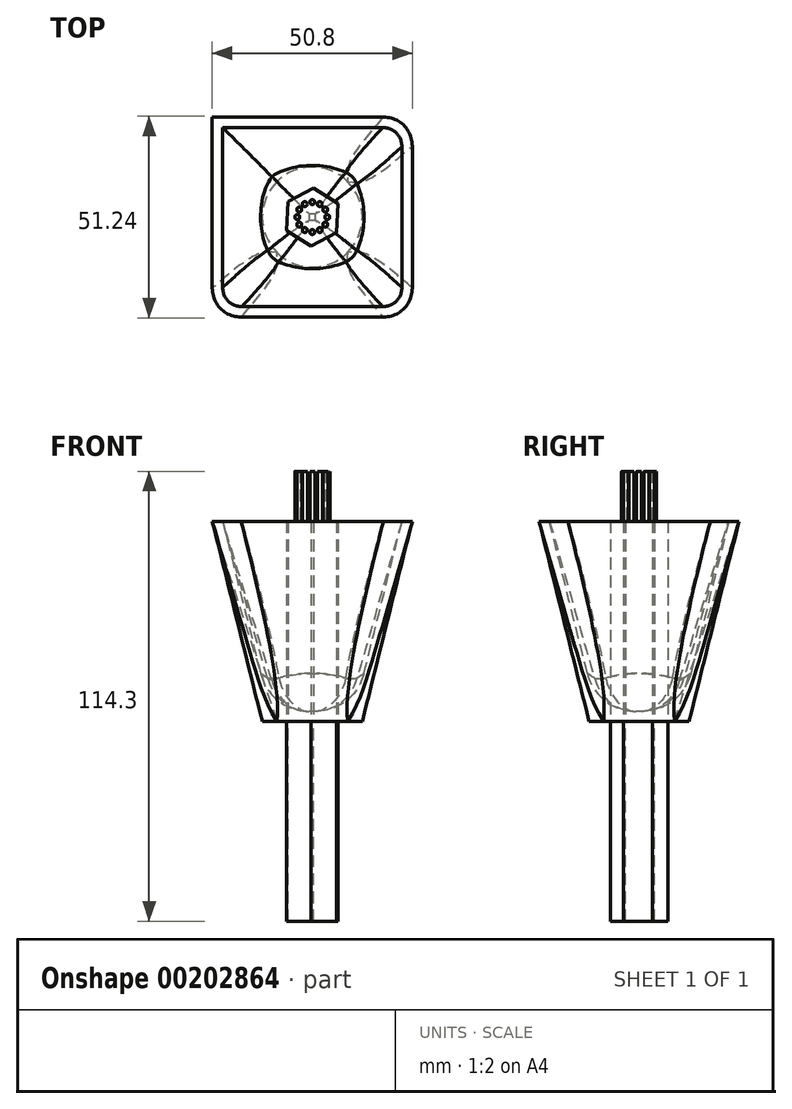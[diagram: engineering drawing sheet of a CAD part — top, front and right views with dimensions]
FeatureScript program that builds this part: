
annotation { "Feature Type Name" : "Feature", "Feature Type Description" : "" }
export const myFeature = defineFeature(function(context is Context, id is Id, definition is map)
    precondition{}
    {
        {
            var Q0;
            Q0=qCreatedBy(makeId("Top.planeOp"),FACE);
            var sketch = newSketch(context, id + "F0", { "sketchPlane" : qUnion([Q0])});
            skCircle(sketch, "E0", {"center": v(0, 0) * mm, "radius": 12.7 * mm});
            skSolve(sketch);
        }
        {
            var Q0;
            Q0=qCreatedBy(makeId("Top.planeOp"),FACE);
            cPlane(context, id + "F1", {"entities" : qUnion([Q0]), "cplaneType" : CPlaneType.OFFSET, "offset" : 50.8 * mm, "width" : 152.4 * mm, "height" : 152.4 * mm});
        }
        {
            var Q0;
            Q0=qCreatedBy(id+"F1.planeOp",FACE);
            var sketch = newSketch(context, id + "F2", { "sketchPlane" : qUnion([Q0])});
            skLineSegment(sketch, "E1.bottom", {"start": v(25.4, 25.4) * mm, "end": v(-25.4, 25.4) * mm});
            skLineSegment(sketch, "E1.top", {"start": v(25.4, -25.4) * mm, "end": v(-25.4, -25.4) * mm});
            skLineSegment(sketch, "E1.left", {"start": v(25.4, 25.4) * mm, "end": v(25.4, -25.4) * mm});
            skLineSegment(sketch, "E1.right", {"start": v(-25.4, 25.4) * mm, "end": v(-25.4, -25.4) * mm});
            skPoint(sketch, "E1.middle", {"position": v(0, 0) * mm});
            skSolve(sketch);
        }
        {
            var Q0;
            Q0=makeQuery(id+"F0.imprint","IMPRINT",FACE,{"disambiguationData":[TD([[makeQuery(id+"F0.imprint","IMPRINT",EDGE,{"derivedFrom":sQuery(id+"F0.wireOp",EDGE,"E0")}),1.0]])]});
            var Q1;
            Q1=makeQuery(id+"F2.imprint","IMPRINT",FACE,{"disambiguationData":[TD([[makeQuery(id+"F2.imprint","IMPRINT",EDGE,{"derivedFrom":sQuery(id+"F2.wireOp",EDGE,"E1.bottom")}),1.0]])]});
            loft(context, id + "F3", {"sheetProfilesArray" : [{ "sheetProfileEntities" : qUnion([Q0]) }, { "sheetProfileEntities" : qUnion([Q1]) }]});
        }
        {
            var Q0;
            Q0=makeQuery(id+"F3.opLoft","SWEPT_EDGE",EDGE,{"disambiguationData":[OSD([sQuery(id+"F0.wireOp",EDGE,"E0"),sQuery(id+"F2.wireOp",EDGE,"E1.bottom"),sQuery(id+"F2.wireOp",EDGE,"E1.left"),sQuery(id+"F2.wireOp",EDGE,"E1.right")])]});
            var Q1;
            Q1=makeQuery(id+"F3.opLoft","SWEPT_EDGE",EDGE,{"disambiguationData":[OSD([sQuery(id+"F2.wireOp",EDGE,"E1.bottom"),sQuery(id+"F2.wireOp",EDGE,"E1.left")])]});
            var Q2;
            Q2=makeQuery(id+"F3.opLoft","SWEPT_EDGE",EDGE,{"disambiguationData":[OSD([sQuery(id+"F0.wireOp",EDGE,"E0"),sQuery(id+"F2.wireOp",EDGE,"E1.top"),sQuery(id+"F2.wireOp",EDGE,"E1.left"),sQuery(id+"F2.wireOp",EDGE,"E1.right")])]});
            var Q3;
            Q3=makeQuery(id+"F3.opLoft","SWEPT_EDGE",EDGE,{"disambiguationData":[OSD([sQuery(id+"F0.wireOp",EDGE,"E0"),sQuery(id+"F2.wireOp",EDGE,"E1.bottom"),sQuery(id+"F2.wireOp",EDGE,"E1.top"),sQuery(id+"F2.wireOp",EDGE,"E1.right")])]});
            fillet(context, id + "F4", {"entities" : qUnion([Q0, Q1, Q2, Q3]), "radius" : 7.62 * mm, "tangentPropagation" : true, "allowEdgeOverflow" : false});
        }
        {
            var Q0;
            Q0=makeQuery(id+"F3.opLoft","CAP_FACE",FACE,{"disambiguationData":[OSD([makeQuery(id+"F2.imprint","IMPRINT",FACE,{"disambiguationData":[TD([[makeQuery(id+"F2.imprint","IMPRINT",EDGE,{"derivedFrom":sQuery(id+"F2.wireOp",EDGE,"E1.bottom")}),1.0]])]})])],"isStart":true});
            shell(context, id + "F5", {"entities" : qUnion([Q0]), "thickness" : 2.54 * mm});
        }
        {
            var Q0;
            Q0=makeQuery(id+"F5.opShell","OFFSET_FACE",FACE,{"disambiguationData":[OSD([makeQuery(id+"F0.imprint","IMPRINT",FACE,{"disambiguationData":[TD([[makeQuery(id+"F0.imprint","IMPRINT",EDGE,{"derivedFrom":sQuery(id+"F0.wireOp",EDGE,"E0")}),1.0]])]})])]});
            fillet(context, id + "F6", {"entities" : qUnion([Q0]), "radius" : 12.7 * mm, "tangentPropagation" : true, "allowEdgeOverflow" : false});
        }
        {
            var Q0;
            Q0=makeQuery(id+"F3.opLoft","CAP_FACE",FACE,{"disambiguationData":[OSD([makeQuery(id+"F0.imprint","IMPRINT",FACE,{"disambiguationData":[TD([[makeQuery(id+"F0.imprint","IMPRINT",EDGE,{"derivedFrom":sQuery(id+"F0.wireOp",EDGE,"E0")}),1.0]])]})])],"isStart":true});
            var sketch = newSketch(context, id + "F7", { "sketchPlane" : qUnion([Q0])});
            skLineSegment(sketch, "E2", {"start": v(0, 0) * mm, "end": v(12.7, 0) * mm});
            skLineSegment(sketch, "E3", {"start": v(0, 0) * mm, "end": v(0, -12.7) * mm});
            skCircle(sketch, "E4.cCircle", {"center": v(0, 0) * mm, "radius": 6.35 * mm, "construction": true});
            skLineSegment(sketch, "E4.0", {"start": v(-6.5, 3.4) * mm, "end": v(-0.3, 7.33) * mm});
            skLineSegment(sketch, "E4.1", {"start": v(-0.3, 7.33) * mm, "end": v(6.2, 3.92) * mm});
            skLineSegment(sketch, "E4.2", {"start": v(6.2, 3.92) * mm, "end": v(6.5, -3.4) * mm});
            skLineSegment(sketch, "E4.3", {"start": v(6.5, -3.4) * mm, "end": v(0.3, -7.33) * mm});
            skLineSegment(sketch, "E4.4", {"start": v(0.3, -7.33) * mm, "end": v(-6.2, -3.92) * mm});
            skLineSegment(sketch, "E4.5", {"start": v(-6.2, -3.92) * mm, "end": v(-6.5, 3.4) * mm});
            skPoint(sketch, "E4.0.midPoint", {"position": v(-3.4, 5.36) * mm});
            skSolve(sketch);
        }
        {
            var Q0;
            Q0=makeQuery(id+"F7.imprint","IMPRINT",FACE,{"disambiguationData":[TD([[makeQuery(id+"F7.imprint","IMPRINT",EDGE,{"derivedFrom":sQuery(id+"F7.wireOp",EDGE,"E4.0")}),-1.0]])]});
            var Q1;
            {var subQ0=sQuery(id+"F7.wireOp",EDGE,"E4.3");Q1=makeQuery(id+"F7.imprint","IMPRINT",FACE,{"disambiguationData":[TD([[makeQuery(id+"F7.imprint","IMPRINT",EDGE,{"derivedFrom":subQ0}),-1.0]])]});}
            extrude(context, id + "F8", {"entities" : qUnion([Q0, Q1]), "depth" : 50.8 * mm});
        }
        {
            var Q0;
            Q0=makeQuery(id+"F8.opExtrude","SWEPT_BODY",BODY,{"disambiguationData":[OSD([sQuery(id+"F7.wireOp",EDGE,"E4.0"),sQuery(id+"F7.wireOp",EDGE,"E4.1"),sQuery(id+"F7.wireOp",EDGE,"E4.2"),sQuery(id+"F7.wireOp",EDGE,"E4.3"),sQuery(id+"F7.wireOp",EDGE,"E4.4"),sQuery(id+"F7.wireOp",EDGE,"E4.5")])]});
            var Q1;
            Q1=qCreatedBy(makeId("Top.planeOp"),FACE);
            mirror(context, id + "F9", {"entities" : qUnion([Q0]), "mirrorPlane" : qUnion([Q1])});
        }
        {
            var Q0;
            Q0=makeQuery(id+"F9.opPattern","COPY",FACE,{"derivedFrom":makeQuery(id+"F8.opExtrude","CAP_FACE",FACE,{"disambiguationData":[OSD([sQuery(id+"F7.wireOp",EDGE,"E4.0"),sQuery(id+"F7.wireOp",EDGE,"E4.1"),sQuery(id+"F7.wireOp",EDGE,"E4.2"),sQuery(id+"F7.wireOp",EDGE,"E4.3"),sQuery(id+"F7.wireOp",EDGE,"E4.4"),sQuery(id+"F7.wireOp",EDGE,"E4.5")])],"isStart":false}),"instanceName":"1"});
            var sketch = newSketch(context, id + "F10", { "sketchPlane" : qUnion([Q0])});
            skCircle(sketch, "E5", {"center": v(0, 0) * mm, "radius": 3.81 * mm, "construction": true});
            skCircle(sketch, "E6", {"center": v(0, 3.81) * mm, "radius": 0.64 * mm});
            skCircle(sketch, "E7.1.1", {"center": v(-1.9, 3.3) * mm, "radius": 0.64 * mm});
            skCircle(sketch, "E7.2.1", {"center": v(-3.3, 1.9) * mm, "radius": 0.64 * mm});
            skCircle(sketch, "E7.3.1", {"center": v(-3.81, 0) * mm, "radius": 0.64 * mm});
            skCircle(sketch, "E7.4.1", {"center": v(-3.3, -1.9) * mm, "radius": 0.64 * mm});
            skCircle(sketch, "E7.5.1", {"center": v(-1.9, -3.3) * mm, "radius": 0.64 * mm});
            skCircle(sketch, "E7.6.1", {"center": v(0, -3.81) * mm, "radius": 0.64 * mm});
            skCircle(sketch, "E7.7.1", {"center": v(1.9, -3.3) * mm, "radius": 0.64 * mm});
            skCircle(sketch, "E7.8.1", {"center": v(3.3, -1.9) * mm, "radius": 0.64 * mm});
            skCircle(sketch, "E7.9.1", {"center": v(3.81, 0) * mm, "radius": 0.64 * mm});
            skCircle(sketch, "E7.10.1", {"center": v(3.3, 1.9) * mm, "radius": 0.64 * mm});
            skCircle(sketch, "E7.11.1", {"center": v(1.9, 3.3) * mm, "radius": 0.64 * mm});
            skSolve(sketch);
        }
        {
            var Q0;
            Q0=makeQuery(id+"F10.imprint","IMPRINT",FACE,{"disambiguationData":[TD([[makeQuery(id+"F10.imprint","IMPRINT",EDGE,{"derivedFrom":sQuery(id+"F10.wireOp",EDGE,"E7.9.1")}),1.0]])]});
            var Q1;
            Q1=makeQuery(id+"F10.imprint","IMPRINT",FACE,{"disambiguationData":[TD([[makeQuery(id+"F10.imprint","IMPRINT",EDGE,{"derivedFrom":sQuery(id+"F10.wireOp",EDGE,"E7.8.1")}),1.0]])]});
            var Q2;
            Q2=makeQuery(id+"F10.imprint","IMPRINT",FACE,{"disambiguationData":[TD([[makeQuery(id+"F10.imprint","IMPRINT",EDGE,{"derivedFrom":sQuery(id+"F10.wireOp",EDGE,"E7.7.1")}),1.0]])]});
            var Q3;
            Q3=makeQuery(id+"F10.imprint","IMPRINT",FACE,{"disambiguationData":[TD([[makeQuery(id+"F10.imprint","IMPRINT",EDGE,{"derivedFrom":sQuery(id+"F10.wireOp",EDGE,"E7.6.1")}),1.0]])]});
            var Q4;
            Q4=makeQuery(id+"F10.imprint","IMPRINT",FACE,{"disambiguationData":[TD([[makeQuery(id+"F10.imprint","IMPRINT",EDGE,{"derivedFrom":sQuery(id+"F10.wireOp",EDGE,"E7.5.1")}),1.0]])]});
            var Q5;
            Q5=makeQuery(id+"F10.imprint","IMPRINT",FACE,{"disambiguationData":[TD([[makeQuery(id+"F10.imprint","IMPRINT",EDGE,{"derivedFrom":sQuery(id+"F10.wireOp",EDGE,"E7.4.1")}),1.0]])]});
            var Q6;
            Q6=makeQuery(id+"F10.imprint","IMPRINT",FACE,{"disambiguationData":[TD([[makeQuery(id+"F10.imprint","IMPRINT",EDGE,{"derivedFrom":sQuery(id+"F10.wireOp",EDGE,"E7.3.1")}),1.0]])]});
            var Q7;
            Q7=makeQuery(id+"F10.imprint","IMPRINT",FACE,{"disambiguationData":[TD([[makeQuery(id+"F10.imprint","IMPRINT",EDGE,{"derivedFrom":sQuery(id+"F10.wireOp",EDGE,"E7.2.1")}),1.0]])]});
            var Q8;
            Q8=makeQuery(id+"F10.imprint","IMPRINT",FACE,{"disambiguationData":[TD([[makeQuery(id+"F10.imprint","IMPRINT",EDGE,{"derivedFrom":sQuery(id+"F10.wireOp",EDGE,"E7.1.1")}),1.0]])]});
            var Q9;
            Q9=makeQuery(id+"F10.imprint","IMPRINT",FACE,{"disambiguationData":[TD([[makeQuery(id+"F10.imprint","IMPRINT",EDGE,{"derivedFrom":sQuery(id+"F10.wireOp",EDGE,"E6")}),1.0]])]});
            var Q10;
            Q10=makeQuery(id+"F10.imprint","IMPRINT",FACE,{"disambiguationData":[TD([[makeQuery(id+"F10.imprint","IMPRINT",EDGE,{"derivedFrom":sQuery(id+"F10.wireOp",EDGE,"E7.11.1")}),1.0]])]});
            var Q11;
            Q11=makeQuery(id+"F10.imprint","IMPRINT",FACE,{"disambiguationData":[TD([[makeQuery(id+"F10.imprint","IMPRINT",EDGE,{"derivedFrom":sQuery(id+"F10.wireOp",EDGE,"E7.10.1")}),1.0]])]});
            var Q12;
            Q12=sQuery(id+"F10.wireOp",EDGE,"E7.3.1");
            var Q13;
            Q13=sQuery(id+"F10.wireOp",EDGE,"E7.2.1");
            var Q14;
            Q14=sQuery(id+"F10.wireOp",EDGE,"E7.1.1");
            var Q15;
            Q15=sQuery(id+"F10.wireOp",EDGE,"E6");
            var Q16;
            Q16=sQuery(id+"F10.wireOp",EDGE,"E7.11.1");
            var Q17;
            Q17=sQuery(id+"F10.wireOp",EDGE,"E7.10.1");
            extrude(context, id + "F11", {"entities" : qUnion([Q0, Q1, Q2, Q3, Q4, Q5, Q6, Q7, Q8, Q9, Q10, Q11]), "operationType" : NewBodyOperationType.ADD, "surfaceEntities" : qUnion([Q12, Q13, Q14, Q15, Q16, Q17]), "depth" : 12.7 * mm});
        }
    });
